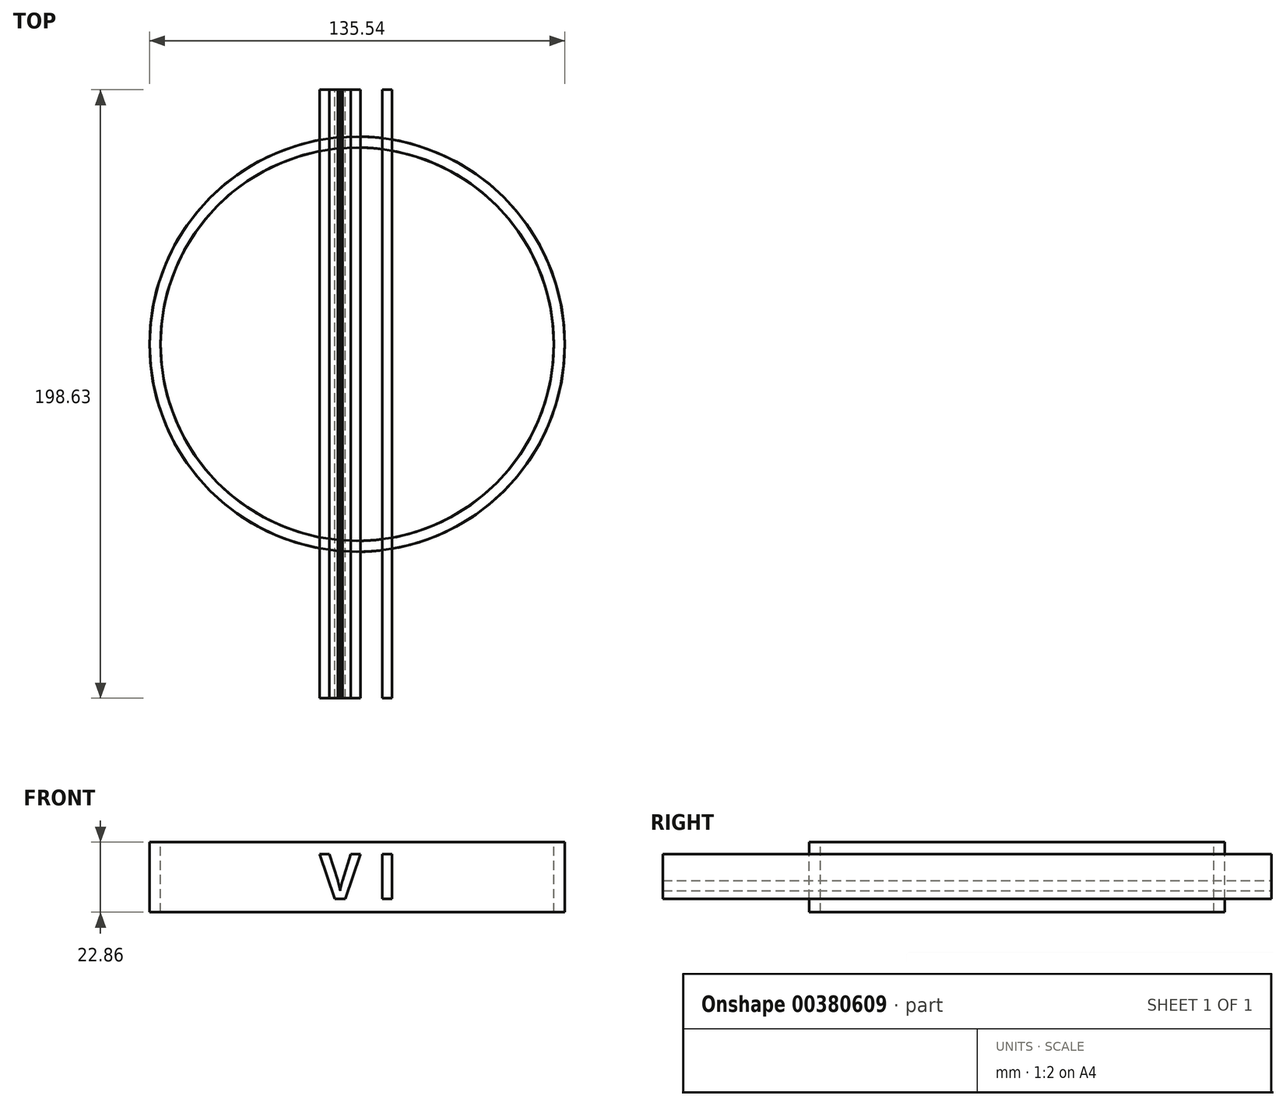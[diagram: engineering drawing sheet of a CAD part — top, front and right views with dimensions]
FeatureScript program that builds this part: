
annotation { "Feature Type Name" : "Feature", "Feature Type Description" : "" }
export const myFeature = defineFeature(function(context is Context, id is Id, definition is map)
    precondition{}
    {
        {
            var Q0;
            Q0=qCreatedBy(makeId("Top.planeOp"),FACE);
            var sketch = newSketch(context, id + "F0", { "sketchPlane" : qUnion([Q0])});
            skCircle(sketch, "E0", {"center": v(0, 0) * mm, "radius": 67.77 * mm});
            skCircle(sketch, "E1", {"center": v(0, 0) * mm, "radius": 64.2 * mm});
            skSolve(sketch);
        }
        {
            var Q0;
            Q0=sQuery(id+"F0.wireOp",EDGE,"E0");
            var Q1;
            Q1=sQuery(id+"F0.wireOp",EDGE,"E1");
            extrude(context, id + "F1", {"bodyType" : ToolBodyType.SURFACE, "surfaceEntities" : qUnion([Q0, Q1]), "depth" : 11.43 * mm, "hasSecondDirection" : true, "secondDirectionOppositeDirection" : true, "secondDirectionDepth" : 11.43 * mm});
        }
        {
            var Q0;
            Q0=qCreatedBy(makeId("Front.planeOp"),FACE);
            var sketch = newSketch(context, id + "F2", { "sketchPlane" : qUnion([Q0])});
            skText(sketch, "E2", { "text": "V I", "fontName": "OpenSans-Bold.ttf"});
            const initialGuessF2  = {"E2": [-0.0122, -0.00706, 1, 0, 0.01472]};
            skSetInitialGuess(sketch, initialGuessF2);
            skSolve(sketch);
        }
        {
            var Q0;
            Q0 = qSketchRegion(id + "F2", true);
            var Q1;
            Q1 = qConstructionFilter(qBodyType(qCreatedBy(id + "F2" ,EDGE), BodyType.WIRE), ConstructionObject.NO);
            extrude(context, id + "F3", {"entities" : qUnion([Q0]), "bodyType" : ToolBodyType.SURFACE, "operationType" : NewBodyOperationType.INTERSECT, "surfaceEntities" : qUnion([Q1]), "oppositeDirection" : true, "depth" : 83.06 * mm, "hasDraft" : true, "draftAngle" : 3 * degree, "hasSecondDirection" : true, "secondDirectionOppositeDirection" : false, "secondDirectionDepth" : 115.57 * mm, "hasSecondDirectionDraft" : true, "secondDirectionDraftAngle" : 3 * degree});
        }
    });
